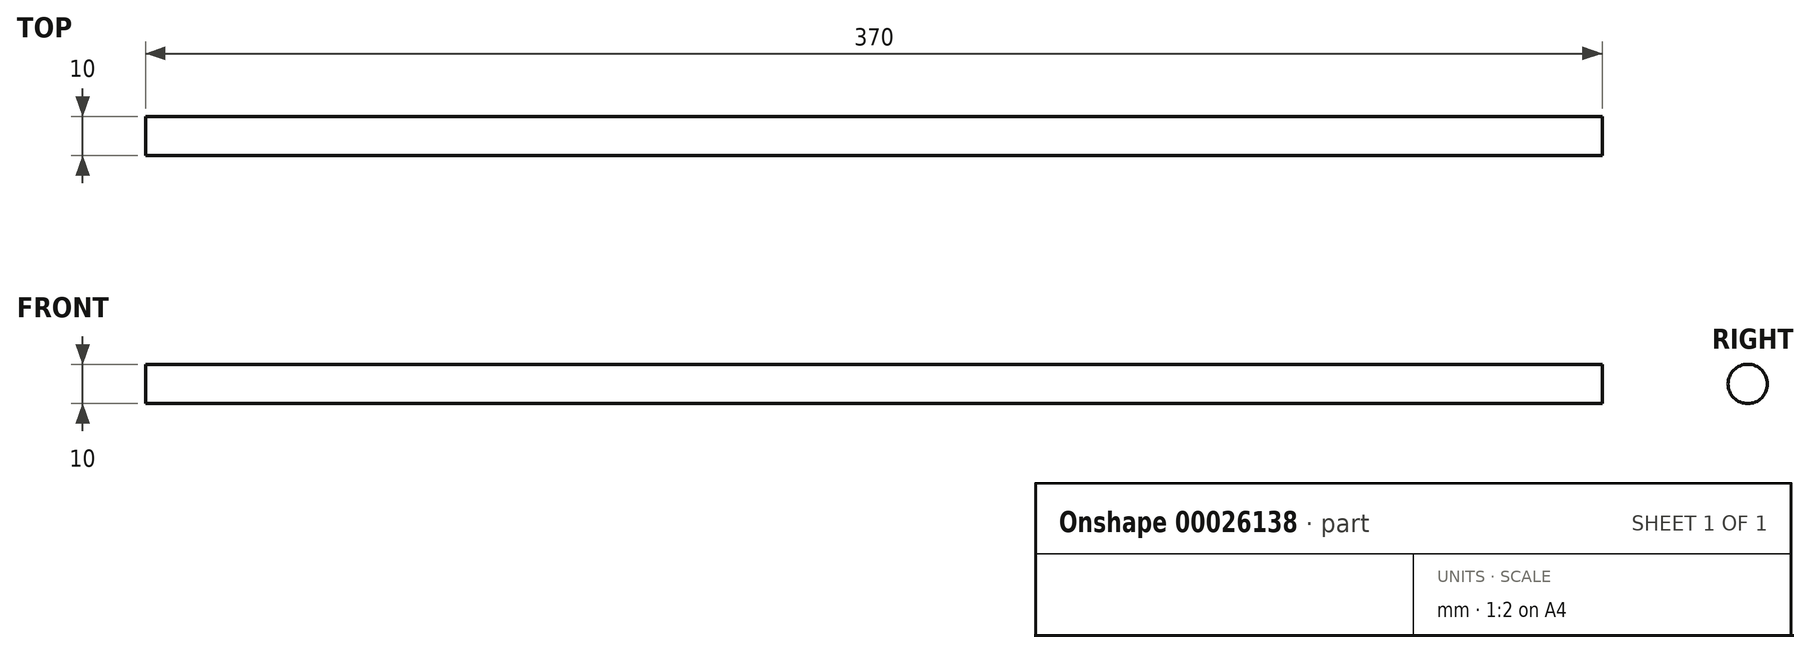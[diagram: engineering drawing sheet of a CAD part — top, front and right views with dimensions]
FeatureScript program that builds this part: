
annotation { "Feature Type Name" : "Feature", "Feature Type Description" : "" }
export const myFeature = defineFeature(function(context is Context, id is Id, definition is map)
    precondition{}
    {
        {
            var Q0;
            Q0=qCreatedBy(makeId("Right.planeOp"),FACE);
            var sketch = newSketch(context, id + "F0", { "sketchPlane" : qUnion([Q0])});
            skCircle(sketch, "E0", {"center": v(0, 0) * mm, "radius": 5 * mm});
            skSolve(sketch);
        }
        {
            var Q0;
            Q0=makeQuery(id+"F0.imprint","IMPRINT",FACE,{"disambiguationData":[TD([[makeQuery(id+"F0.imprint","IMPRINT",EDGE,{"derivedFrom":sQuery(id+"F0.wireOp",EDGE,"E0")}),1.0]])]});
            extrude(context, id + "F1", {"entities" : qUnion([Q0]), "depth" : 370 * mm});
        }
    });
